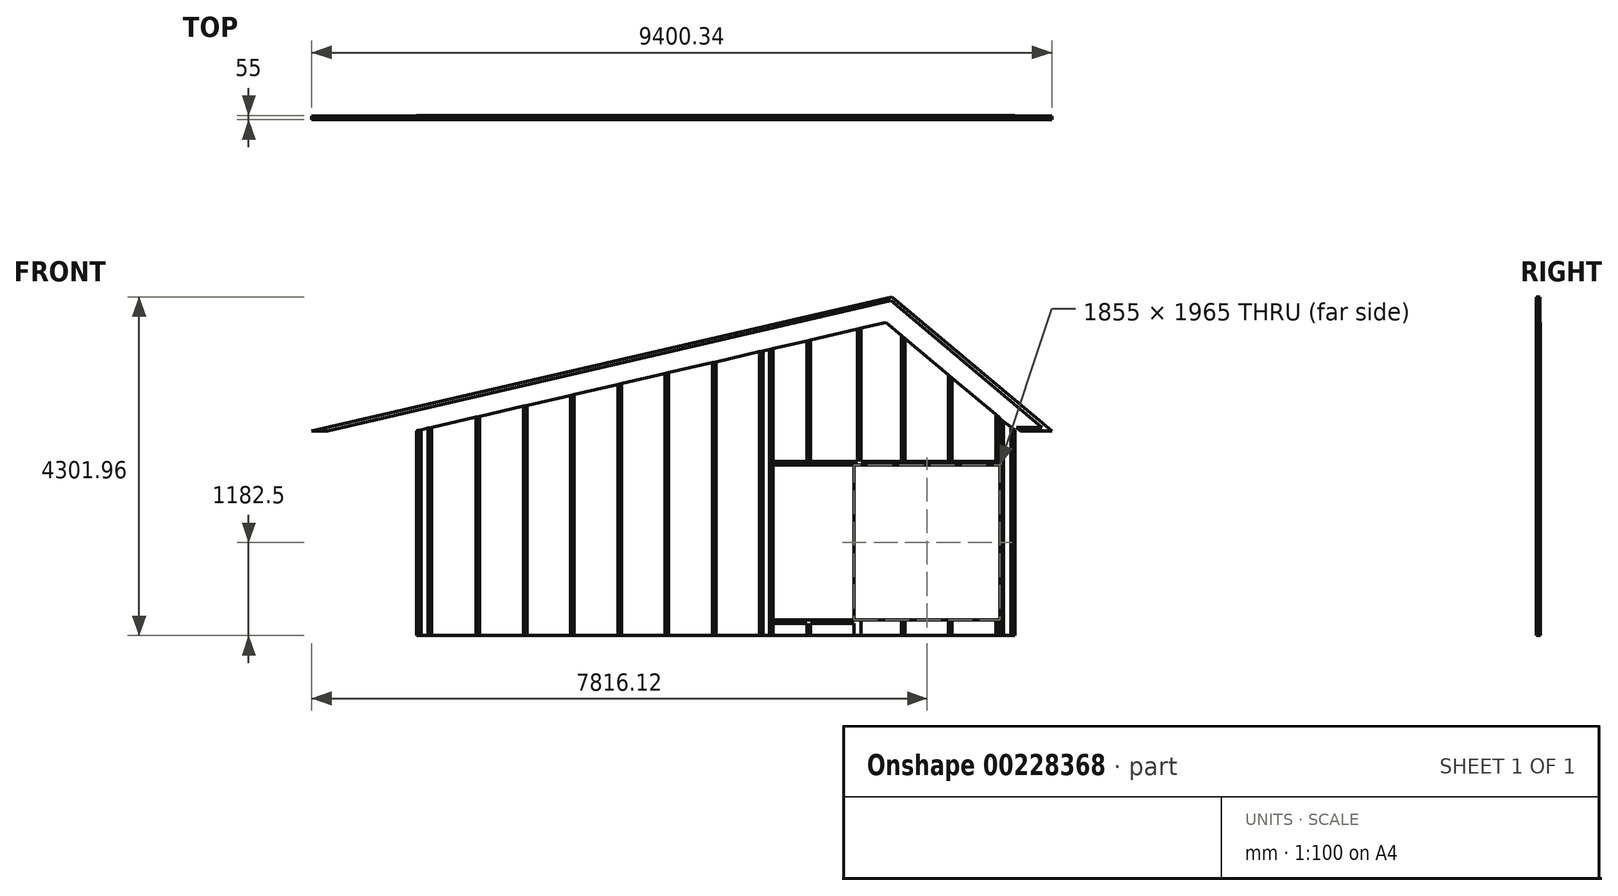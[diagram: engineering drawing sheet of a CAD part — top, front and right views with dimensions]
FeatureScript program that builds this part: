
annotation { "Feature Type Name" : "Feature", "Feature Type Description" : "" }
export const myFeature = defineFeature(function(context is Context, id is Id, definition is map)
    precondition{}
    {
        {
            var Q0;
            Q0=qCreatedBy(makeId("Front.planeOp"),FACE);
            var sketch = newSketch(context, id + "F0", { "sketchPlane" : qUnion([Q0])});
            skLineSegment(sketch, "E0", {"start": v(0, 2907.9) * mm, "end": v(6038.4, 4301.96) * mm});
            skLineSegment(sketch, "E1", {"start": v(7600, 0) * mm, "end": v(0, 0) * mm});
            skLineSegment(sketch, "E2", {"start": v(200, 0) * mm, "end": v(200, 2646.17) * mm});
            skLineSegment(sketch, "E3", {"start": v(0, 2600) * mm, "end": v(5960.14, 3976) * mm});
            skLineSegment(sketch, "E4", {"start": v(5960.14, 3976) * mm, "end": v(7600, 2600) * mm});
            skLineSegment(sketch, "E5", {"start": v(7445, 200) * mm, "end": v(200, 200) * mm});
            skLineSegment(sketch, "E6", {"start": v(0, 2907.9) * mm, "end": v(-1333.62, 2600) * mm});
            skLineSegment(sketch, "E7", {"start": v(-1333.62, 2600) * mm, "end": v(0, 2600) * mm});
            skLineSegment(sketch, "E8", {"start": v(755, 200) * mm, "end": v(755, 2774.3) * mm});
            skLineSegment(sketch, "E9", {"start": v(755, 2774.3) * mm, "end": v(800, 2784.7) * mm});
            skLineSegment(sketch, "E10", {"start": v(800, 2784.7) * mm, "end": v(800, 200) * mm});
            skLineSegment(sketch, "E11", {"start": v(1355, 2912.83) * mm, "end": v(1355, 200) * mm});
            skLineSegment(sketch, "E12", {"start": v(1400, 2923.22) * mm, "end": v(1400, 200) * mm});
            skLineSegment(sketch, "E13", {"start": v(1955, 3051.35) * mm, "end": v(1955, 200) * mm});
            skLineSegment(sketch, "E14", {"start": v(2000, 3061.74) * mm, "end": v(2000, 200) * mm});
            skLineSegment(sketch, "E15", {"start": v(2555, 3189.87) * mm, "end": v(2555, 200) * mm});
            skLineSegment(sketch, "E16", {"start": v(2600, 200) * mm, "end": v(2600, 3200.26) * mm});
            skLineSegment(sketch, "E17", {"start": v(3755, 3466.91) * mm, "end": v(3755, 200) * mm});
            skLineSegment(sketch, "E18", {"start": v(3800, 200) * mm, "end": v(3800, 3477.3) * mm});
            skLineSegment(sketch, "E19", {"start": v(3155, 3328.39) * mm, "end": v(3155, 200) * mm});
            skLineSegment(sketch, "E20", {"start": v(3200, 200) * mm, "end": v(3200, 3338.78) * mm});
            skLineSegment(sketch, "E21", {"start": v(4355, 3605.43) * mm, "end": v(4355, 200) * mm});
            skLineSegment(sketch, "E22", {"start": v(4400, 3615.82) * mm, "end": v(4400, 200) * mm});
            skLineSegment(sketch, "E23", {"start": v(4955, 200) * mm, "end": v(4955, 3743.95) * mm});
            skLineSegment(sketch, "E24", {"start": v(5000, 3754.34) * mm, "end": v(5000, 200) * mm});
            skLineSegment(sketch, "E25", {"start": v(5555, 3882.47) * mm, "end": v(5555, 200) * mm});
            skLineSegment(sketch, "E26", {"start": v(5600, 200) * mm, "end": v(5600, 3892.86) * mm});
            skLineSegment(sketch, "E27", {"start": v(6155, 3812.5) * mm, "end": v(6155, 200) * mm});
            skLineSegment(sketch, "E28", {"start": v(6200, 3774.74) * mm, "end": v(6200, 200) * mm});
            skLineSegment(sketch, "E29", {"start": v(6755, 200) * mm, "end": v(6755, 3309.04) * mm});
            skLineSegment(sketch, "E30", {"start": v(6800, 3271.28) * mm, "end": v(6800, 200) * mm});
            skLineSegment(sketch, "E31", {"start": v(7355, 200) * mm, "end": v(7355, 2805.58) * mm});
            skLineSegment(sketch, "E32", {"start": v(7400, 2767.82) * mm, "end": v(7400, 200) * mm});
            skLineSegment(sketch, "E33", {"start": v(-1133.58, 2600) * mm, "end": v(6026.66, 4253.07) * mm});
            skLineSegment(sketch, "E34", {"start": v(200, 155) * mm, "end": v(7445, 155) * mm});
            skLineSegment(sketch, "E35", {"start": v(7445, 45) * mm, "end": v(200, 45) * mm});
            skLineSegment(sketch, "E36", {"start": v(-938.66, 2645) * mm, "end": v(-5.13, 2645) * mm});
            skLineSegment(sketch, "E37", {"start": v(-5.13, 2645) * mm, "end": v(5971.88, 4024.9) * mm});
            skLineSegment(sketch, "E38", {"start": v(0, 2600) * mm, "end": v(0, 0) * mm});
            skLineSegment(sketch, "E39", {"start": v(45, 0) * mm, "end": v(45, 2610.39) * mm});
            skLineSegment(sketch, "E40", {"start": v(155, 0) * mm, "end": v(155, 2635.78) * mm});
            skLineSegment(sketch, "E41.trimOffspring", {"start": v(7600, 2600) * mm, "end": v(7600, 0) * mm});
            skLineSegment(sketch, "E42", {"start": v(7445, 0) * mm, "end": v(7445, 2730.06) * mm});
            skLineSegment(sketch, "E43", {"start": v(7555, 0) * mm, "end": v(7555, 2637.76) * mm});
            skLineSegment(sketch, "E44", {"start": v(6038.4, 4301.96) * mm, "end": v(8066.72, 2600) * mm});
            skLineSegment(sketch, "E45", {"start": v(8066.72, 2600) * mm, "end": v(7600, 2600) * mm});
            skLineSegment(sketch, "E46", {"start": v(6026.66, 4253.07) * mm, "end": v(7996.7, 2600) * mm});
            skLineSegment(sketch, "E47", {"start": v(5971.88, 4024.9) * mm, "end": v(7670, 2600) * mm});
            skLineSegment(sketch, "E48", {"start": v(7616.38, 2645) * mm, "end": v(7943.08, 2645) * mm});
            skLineSegment(sketch, "E49", {"start": v(6038.4, 4301.96) * mm, "end": v(5960.14, 3976) * mm});
            skSolve(sketch);
        }
        {
            var Q0;
            {var subQ0=sQuery(id+"F0.wireOp",EDGE,"E31");Q0=makeQuery(id+"F0.imprint","IMPRINT",FACE,{"disambiguationData":[TD([[makeQuery(id+"F0.imprint","IMPRINT",EDGE,{"derivedFrom":subQ0}),-1.0]])]});}
            var Q1;
            {var subQ0=sQuery(id+"F0.wireOp",EDGE,"E13");Q1=makeQuery(id+"F0.imprint","IMPRINT",FACE,{"disambiguationData":[TD([[makeQuery(id+"F0.imprint","IMPRINT",EDGE,{"derivedFrom":subQ0}),1.0]])]});}
            var Q2;
            {var subQ0=sQuery(id+"F0.wireOp",EDGE,"E17");Q2=makeQuery(id+"F0.imprint","IMPRINT",FACE,{"disambiguationData":[TD([[makeQuery(id+"F0.imprint","IMPRINT",EDGE,{"derivedFrom":subQ0}),-1.0]])]});}
            var Q3;
            {var subQ2=sQuery(id+"F0.wireOp",EDGE,"E25");Q3=makeQuery(id+"F0.imprint","IMPRINT",FACE,{"disambiguationData":[TD([[makeQuery(id+"F0.imprint","IMPRINT",EDGE,{"derivedFrom":subQ2}),1.0]])]});}
            var Q4;
            {var subQ0=sQuery(id+"F0.wireOp",EDGE,"E18");Q4=makeQuery(id+"F0.imprint","IMPRINT",FACE,{"disambiguationData":[TD([[makeQuery(id+"F0.imprint","IMPRINT",EDGE,{"derivedFrom":subQ0}),-1.0]])]});}
            var Q5;
            {var subQ0=sQuery(id+"F0.wireOp",EDGE,"E14");Q5=makeQuery(id+"F0.imprint","IMPRINT",FACE,{"disambiguationData":[TD([[makeQuery(id+"F0.imprint","IMPRINT",EDGE,{"derivedFrom":subQ0}),1.0]])]});}
            var Q6;
            {var subQ5=sQuery(id+"F0.wireOp",EDGE,"E8");Q6=makeQuery(id+"F0.imprint","IMPRINT",FACE,{"disambiguationData":[TD([[makeQuery(id+"F0.imprint","IMPRINT",EDGE,{"derivedFrom":subQ5}),1.0]])]});}
            var Q7;
            {var subQ0=sQuery(id+"F0.wireOp",EDGE,"E28");Q7=makeQuery(id+"F0.imprint","IMPRINT",FACE,{"disambiguationData":[TD([[makeQuery(id+"F0.imprint","IMPRINT",EDGE,{"derivedFrom":subQ0}),1.0]])]});}
            var Q8;
            {var subQ0=sQuery(id+"F0.wireOp",EDGE,"E30");Q8=makeQuery(id+"F0.imprint","IMPRINT",FACE,{"disambiguationData":[TD([[makeQuery(id+"F0.imprint","IMPRINT",EDGE,{"derivedFrom":subQ0}),1.0]])]});}
            var Q9;
            {var subQ0=sQuery(id+"F0.wireOp",EDGE,"E26");Q9=makeQuery(id+"F0.imprint","IMPRINT",FACE,{"disambiguationData":[TD([[makeQuery(id+"F0.imprint","IMPRINT",EDGE,{"derivedFrom":subQ0}),-1.0]])]});}
            var Q10;
            {var subQ0=sQuery(id+"F0.wireOp",EDGE,"E16");Q10=makeQuery(id+"F0.imprint","IMPRINT",FACE,{"disambiguationData":[TD([[makeQuery(id+"F0.imprint","IMPRINT",EDGE,{"derivedFrom":subQ0}),-1.0]])]});}
            var Q11;
            {var subQ0=sQuery(id+"F0.wireOp",EDGE,"E12");Q11=makeQuery(id+"F0.imprint","IMPRINT",FACE,{"disambiguationData":[TD([[makeQuery(id+"F0.imprint","IMPRINT",EDGE,{"derivedFrom":subQ0}),1.0]])]});}
            var Q12;
            {var subQ0=sQuery(id+"F0.wireOp",EDGE,"E24");Q12=makeQuery(id+"F0.imprint","IMPRINT",FACE,{"disambiguationData":[TD([[makeQuery(id+"F0.imprint","IMPRINT",EDGE,{"derivedFrom":subQ0}),1.0]])]});}
            var Q13;
            {var subQ0=sQuery(id+"F0.wireOp",EDGE,"E17");Q13=makeQuery(id+"F0.imprint","IMPRINT",FACE,{"disambiguationData":[TD([[makeQuery(id+"F0.imprint","IMPRINT",EDGE,{"derivedFrom":subQ0}),1.0]])]});}
            var Q14;
            {var subQ0=sQuery(id+"F0.wireOp",EDGE,"E10");Q14=makeQuery(id+"F0.imprint","IMPRINT",FACE,{"disambiguationData":[TD([[makeQuery(id+"F0.imprint","IMPRINT",EDGE,{"derivedFrom":subQ0}),1.0]])]});}
            var Q15;
            {var subQ0=sQuery(id+"F0.wireOp",EDGE,"E22");Q15=makeQuery(id+"F0.imprint","IMPRINT",FACE,{"disambiguationData":[TD([[makeQuery(id+"F0.imprint","IMPRINT",EDGE,{"derivedFrom":subQ0}),1.0]])]});}
            var Q16;
            {var subQ0=sQuery(id+"F0.wireOp",EDGE,"E11");Q16=makeQuery(id+"F0.imprint","IMPRINT",FACE,{"disambiguationData":[TD([[makeQuery(id+"F0.imprint","IMPRINT",EDGE,{"derivedFrom":subQ0}),1.0]])]});}
            var Q17;
            {var subQ2=sQuery(id+"F0.wireOp",EDGE,"E23");Q17=makeQuery(id+"F0.imprint","IMPRINT",FACE,{"disambiguationData":[TD([[makeQuery(id+"F0.imprint","IMPRINT",EDGE,{"derivedFrom":subQ2}),-1.0]])]});}
            var Q18;
            {var subQ0=sQuery(id+"F0.wireOp",EDGE,"E21");Q18=makeQuery(id+"F0.imprint","IMPRINT",FACE,{"disambiguationData":[TD([[makeQuery(id+"F0.imprint","IMPRINT",EDGE,{"derivedFrom":subQ0}),1.0]])]});}
            var Q19;
            {var subQ0=sQuery(id+"F0.wireOp",EDGE,"E19");Q19=makeQuery(id+"F0.imprint","IMPRINT",FACE,{"disambiguationData":[TD([[makeQuery(id+"F0.imprint","IMPRINT",EDGE,{"derivedFrom":subQ0}),1.0]])]});}
            var Q20;
            {var subQ2=sQuery(id+"F0.wireOp",EDGE,"E29");Q20=makeQuery(id+"F0.imprint","IMPRINT",FACE,{"disambiguationData":[TD([[makeQuery(id+"F0.imprint","IMPRINT",EDGE,{"derivedFrom":subQ2}),-1.0]])]});}
            var Q21;
            {var subQ2=sQuery(id+"F0.wireOp",EDGE,"E27");Q21=makeQuery(id+"F0.imprint","IMPRINT",FACE,{"disambiguationData":[TD([[makeQuery(id+"F0.imprint","IMPRINT",EDGE,{"derivedFrom":subQ2}),1.0]])]});}
            var Q22;
            {var subQ0=sQuery(id+"F0.wireOp",EDGE,"E8");Q22=makeQuery(id+"F0.imprint","IMPRINT",FACE,{"disambiguationData":[TD([[makeQuery(id+"F0.imprint","IMPRINT",EDGE,{"derivedFrom":subQ0}),-1.0]])]});}
            var Q23;
            {var subQ0=sQuery(id+"F0.wireOp",EDGE,"E15");Q23=makeQuery(id+"F0.imprint","IMPRINT",FACE,{"disambiguationData":[TD([[makeQuery(id+"F0.imprint","IMPRINT",EDGE,{"derivedFrom":subQ0}),1.0]])]});}
            var Q24;
            {var subQ6=sQuery(id+"F0.wireOp",EDGE,"E40");Q24=makeQuery(id+"F0.imprint","IMPRINT",FACE,{"disambiguationData":[TD([[makeQuery(id+"F0.imprint","IMPRINT",EDGE,{"derivedFrom":subQ6}),-1.0]])]});}
            var Q25;
            {var subQ0=sQuery(id+"F0.wireOp",EDGE,"E39");Q25=makeQuery(id+"F0.imprint","IMPRINT",FACE,{"disambiguationData":[TD([[makeQuery(id+"F0.imprint","IMPRINT",EDGE,{"derivedFrom":subQ0}),-1.0]])]});}
            var Q26;
            {var subQ0=sQuery(id+"F0.wireOp",EDGE,"E38");Q26=makeQuery(id+"F0.imprint","IMPRINT",FACE,{"disambiguationData":[TD([[makeQuery(id+"F0.imprint","IMPRINT",EDGE,{"derivedFrom":subQ0}),1.0]])]});}
            var Q27;
            {var subQ6=sQuery(id+"F0.wireOp",EDGE,"E43");Q27=makeQuery(id+"F0.imprint","IMPRINT",FACE,{"disambiguationData":[TD([[makeQuery(id+"F0.imprint","IMPRINT",EDGE,{"derivedFrom":subQ6}),1.0]])]});}
            var Q28;
            {var subQ0=sQuery(id+"F0.wireOp",EDGE,"E32");Q28=makeQuery(id+"F0.imprint","IMPRINT",FACE,{"disambiguationData":[TD([[makeQuery(id+"F0.imprint","IMPRINT",EDGE,{"derivedFrom":subQ0}),1.0]])]});}
            var Q29;
            {var subQ2=sQuery(id+"F0.wireOp",EDGE,"E41.trimOffspring");Q29=makeQuery(id+"F0.imprint","IMPRINT",FACE,{"disambiguationData":[TD([[makeQuery(id+"F0.imprint","IMPRINT",EDGE,{"derivedFrom":subQ2}),-1.0]])]});}
            var Q30;
            {var subQ10=sQuery(id+"F0.wireOp",EDGE,"E34");Q30=makeQuery(id+"F0.imprint","IMPRINT",FACE,{"disambiguationData":[TD([[makeQuery(id+"F0.imprint","IMPRINT",EDGE,{"derivedFrom":subQ10}),1.0]])]});}
            var Q31;
            {var subQ2=sQuery(id+"F0.wireOp",EDGE,"E34");Q31=makeQuery(id+"F0.imprint","IMPRINT",FACE,{"disambiguationData":[TD([[makeQuery(id+"F0.imprint","IMPRINT",EDGE,{"derivedFrom":subQ2}),-1.0]])]});}
            var Q32;
            {var subQ5=sQuery(id+"F0.wireOp",EDGE,"E35");Q32=makeQuery(id+"F0.imprint","IMPRINT",FACE,{"disambiguationData":[TD([[makeQuery(id+"F0.imprint","IMPRINT",EDGE,{"derivedFrom":subQ5}),1.0]])]});}
            extrude(context, id + "F1", {"entities" : qUnion([Q0, Q1, Q2, Q3, Q4, Q5, Q6, Q7, Q8, Q9, Q10, Q11, Q12, Q13, Q14, Q15, Q16, Q17, Q18, Q19, Q20, Q21, Q22, Q23, Q24, Q25, Q26, Q27, Q28, Q29, Q30, Q31, Q32]), "depth" : 10 * mm, "offsetDistance" : 25 * mm});
        }
        {
            var Q0;
            Q0=makeQuery(id+"F1.opExtrude","CAP_FACE",FACE,{"disambiguationData":[OSD([sQuery(id+"F0.wireOp",EDGE,"E0"),sQuery(id+"F0.wireOp",EDGE,"E1"),sQuery(id+"F0.wireOp",EDGE,"E6"),sQuery(id+"F0.wireOp",EDGE,"E7"),sQuery(id+"F0.wireOp",EDGE,"E38"),sQuery(id+"F0.wireOp",EDGE,"E41.trimOffspring"),sQuery(id+"F0.wireOp",EDGE,"E44"),sQuery(id+"F0.wireOp",EDGE,"E45")])],"isStart":false});
            var sketch = newSketch(context, id + "F2", { "sketchPlane" : qUnion([Q0])});
            skLineSegment(sketch, "E50", {"start": v(0, 2907.9) * mm, "end": v(6038.4, 4301.96) * mm});
            skLineSegment(sketch, "E51", {"start": v(7600, 0) * mm, "end": v(0, 0) * mm});
            skLineSegment(sketch, "E52", {"start": v(200, 0) * mm, "end": v(200, 2646.17) * mm});
            skLineSegment(sketch, "E53", {"start": v(0, 2600) * mm, "end": v(5960.14, 3976) * mm});
            skLineSegment(sketch, "E54", {"start": v(5960.14, 3976) * mm, "end": v(7600, 2600) * mm});
            skLineSegment(sketch, "E55", {"start": v(0, 2907.9) * mm, "end": v(-1333.62, 2600) * mm});
            skLineSegment(sketch, "E56", {"start": v(-1333.62, 2600) * mm, "end": v(0, 2600) * mm});
            skLineSegment(sketch, "E57", {"start": v(755, 0) * mm, "end": v(755, 2774.3) * mm});
            skLineSegment(sketch, "E58", {"start": v(755, 2774.3) * mm, "end": v(800, 2784.7) * mm});
            skLineSegment(sketch, "E59", {"start": v(800, 2784.7) * mm, "end": v(800, 0) * mm});
            skLineSegment(sketch, "E60", {"start": v(1355, 2912.83) * mm, "end": v(1355, 0) * mm});
            skLineSegment(sketch, "E61", {"start": v(1400, 2923.22) * mm, "end": v(1400, 0) * mm});
            skLineSegment(sketch, "E62", {"start": v(1955, 3051.35) * mm, "end": v(1955, 0) * mm});
            skLineSegment(sketch, "E63", {"start": v(2000, 3061.74) * mm, "end": v(2000, 0) * mm});
            skLineSegment(sketch, "E64", {"start": v(2555, 3189.87) * mm, "end": v(2555, 0) * mm});
            skLineSegment(sketch, "E65", {"start": v(2600, 0) * mm, "end": v(2600, 3200.26) * mm});
            skLineSegment(sketch, "E66", {"start": v(3755, 3466.91) * mm, "end": v(3755, 0) * mm});
            skLineSegment(sketch, "E67", {"start": v(3800, 0) * mm, "end": v(3800, 3477.3) * mm});
            skLineSegment(sketch, "E68", {"start": v(3155, 3328.39) * mm, "end": v(3155, 0) * mm});
            skLineSegment(sketch, "E69", {"start": v(3200, 0) * mm, "end": v(3200, 3338.78) * mm});
            skLineSegment(sketch, "E70", {"start": v(4355, 3605.43) * mm, "end": v(4355, 0) * mm});
            skLineSegment(sketch, "E71", {"start": v(4400, 3615.82) * mm, "end": v(4400, 0) * mm});
            skLineSegment(sketch, "E72", {"start": v(4955, 0) * mm, "end": v(4955, 3743.95) * mm});
            skLineSegment(sketch, "E73", {"start": v(5000, 3754.34) * mm, "end": v(5000, 0) * mm});
            skLineSegment(sketch, "E74", {"start": v(5555, 3882.47) * mm, "end": v(5555, 0) * mm});
            skLineSegment(sketch, "E75", {"start": v(5600, 0) * mm, "end": v(5600, 3892.86) * mm});
            skLineSegment(sketch, "E76", {"start": v(6155, 3812.5) * mm, "end": v(6155, 0) * mm});
            skLineSegment(sketch, "E77", {"start": v(6200, 3774.74) * mm, "end": v(6200, 0) * mm});
            skLineSegment(sketch, "E78", {"start": v(6755, 0) * mm, "end": v(6755, 3309.04) * mm});
            skLineSegment(sketch, "E79", {"start": v(6800, 3271.28) * mm, "end": v(6800, 0) * mm});
            skLineSegment(sketch, "E80", {"start": v(7355, 0) * mm, "end": v(7355, 2805.58) * mm});
            skLineSegment(sketch, "E81", {"start": v(7400, 2767.82) * mm, "end": v(7400, 0) * mm});
            skLineSegment(sketch, "E82", {"start": v(-1133.58, 2600) * mm, "end": v(6026.66, 4253.07) * mm});
            skLineSegment(sketch, "E83", {"start": v(-938.66, 2645) * mm, "end": v(-5.13, 2645) * mm});
            skLineSegment(sketch, "E84", {"start": v(-5.13, 2645) * mm, "end": v(5971.88, 4024.9) * mm});
            skLineSegment(sketch, "E85", {"start": v(0, 2600) * mm, "end": v(0, 0) * mm});
            skLineSegment(sketch, "E86", {"start": v(55, 0) * mm, "end": v(55, 2612.7) * mm});
            skLineSegment(sketch, "E87", {"start": v(145, 0) * mm, "end": v(145, 2633.48) * mm});
            skLineSegment(sketch, "E88.trimOffspring", {"start": v(7600, 2600) * mm, "end": v(7600, 0) * mm});
            skLineSegment(sketch, "E89", {"start": v(7455, 0) * mm, "end": v(7455, 2721.67) * mm});
            skLineSegment(sketch, "E90", {"start": v(6038.4, 4301.96) * mm, "end": v(8066.72, 2600) * mm});
            skLineSegment(sketch, "E91", {"start": v(8066.72, 2600) * mm, "end": v(7600, 2600) * mm});
            skLineSegment(sketch, "E92", {"start": v(6026.66, 4253.07) * mm, "end": v(7996.7, 2600) * mm});
            skLineSegment(sketch, "E93", {"start": v(5971.88, 4024.9) * mm, "end": v(7670, 2600) * mm});
            skLineSegment(sketch, "E94", {"start": v(7616.38, 2645) * mm, "end": v(7943.08, 2645) * mm});
            skLineSegment(sketch, "E95", {"start": v(7400, 1090) * mm, "end": v(5645, 1090) * mm});
            skLineSegment(sketch, "E96", {"start": v(4525, 2165) * mm, "end": v(7410, 2165) * mm});
            skLineSegment(sketch, "E97", {"start": v(7410, 2210) * mm, "end": v(4525, 2210) * mm});
            skLineSegment(sketch, "E98", {"start": v(5645, 3903.25) * mm, "end": v(5645, 0) * mm});
            skLineSegment(sketch, "E99", {"start": v(5645, 1045) * mm, "end": v(7400, 1045) * mm});
            skLineSegment(sketch, "E100", {"start": v(4525, 3644.68) * mm, "end": v(4525, 0) * mm});
            skLineSegment(sketch, "E101", {"start": v(4480, 3634.29) * mm, "end": v(4480, 0) * mm});
            skLineSegment(sketch, "E102", {"start": v(4525, 200) * mm, "end": v(5555, 200) * mm});
            skLineSegment(sketch, "E103", {"start": v(5555, 155) * mm, "end": v(4525, 155) * mm});
            skLineSegment(sketch, "E104", {"start": v(10, 2602.3) * mm, "end": v(10, 0) * mm});
            skLineSegment(sketch, "E105", {"start": v(10, 0) * mm, "end": v(190, 0) * mm});
            skLineSegment(sketch, "E106", {"start": v(190, 0) * mm, "end": v(190, 2643.86) * mm});
            skLineSegment(sketch, "E107", {"start": v(745, 2772) * mm, "end": v(745, 0) * mm});
            skLineSegment(sketch, "E108", {"start": v(810, 0) * mm, "end": v(810, 2787) * mm});
            skLineSegment(sketch, "E109", {"start": v(1345, 2910.52) * mm, "end": v(1345, 0) * mm});
            skLineSegment(sketch, "E110", {"start": v(1410, 2925.52) * mm, "end": v(1410, 0) * mm});
            skLineSegment(sketch, "E111", {"start": v(1945, 3049.04) * mm, "end": v(1945, 0) * mm});
            skLineSegment(sketch, "E112", {"start": v(2010, 3064.05) * mm, "end": v(2010, 0) * mm});
            skLineSegment(sketch, "E113", {"start": v(2545, 3187.56) * mm, "end": v(2545, 0) * mm});
            skLineSegment(sketch, "E114", {"start": v(2610, 3202.57) * mm, "end": v(2610, 0) * mm});
            skLineSegment(sketch, "E115", {"start": v(3145, 3326.08) * mm, "end": v(3145, 0) * mm});
            skLineSegment(sketch, "E116", {"start": v(3210, 3341.09) * mm, "end": v(3210, 0) * mm});
            skLineSegment(sketch, "E117", {"start": v(3745, 3464.6) * mm, "end": v(3745, 0) * mm});
            skLineSegment(sketch, "E118", {"start": v(3810, 3479.6) * mm, "end": v(3810, 0) * mm});
            skLineSegment(sketch, "E119", {"start": v(4345, 3603.12) * mm, "end": v(4345, 0) * mm});
            skLineSegment(sketch, "E120", {"start": v(4410, 0) * mm, "end": v(4410, 3618.13) * mm});
            skLineSegment(sketch, "E121", {"start": v(4470, 3631.98) * mm, "end": v(4470, 0) * mm});
            skLineSegment(sketch, "E122", {"start": v(4535, 0) * mm, "end": v(4535, 3646.99) * mm});
            skLineSegment(sketch, "E123", {"start": v(4535, 2220) * mm, "end": v(7410, 2220) * mm});
            skLineSegment(sketch, "E124", {"start": v(5645, 2155) * mm, "end": v(7410, 2155) * mm});
            skLineSegment(sketch, "E125", {"start": v(5645, 1100) * mm, "end": v(7400, 1100) * mm});
            skLineSegment(sketch, "E126", {"start": v(5655, 2155) * mm, "end": v(5655, 1100) * mm});
            skLineSegment(sketch, "E127", {"start": v(5655, 1045) * mm, "end": v(5655, 0) * mm});
            skLineSegment(sketch, "E128", {"start": v(7345, 1045) * mm, "end": v(7345, 0) * mm});
            skLineSegment(sketch, "E129", {"start": v(6145, 1045) * mm, "end": v(6145, 0) * mm});
            skLineSegment(sketch, "E130", {"start": v(6210, 1045) * mm, "end": v(6210, 0) * mm});
            skLineSegment(sketch, "E131", {"start": v(6745, 1045) * mm, "end": v(6745, 0) * mm});
            skLineSegment(sketch, "E132", {"start": v(6810, 1045) * mm, "end": v(6810, 0) * mm});
            skLineSegment(sketch, "E133", {"start": v(4945, 3741.64) * mm, "end": v(4945, 2220) * mm});
            skLineSegment(sketch, "E134", {"start": v(5010, 3756.65) * mm, "end": v(5010, 2220) * mm});
            skLineSegment(sketch, "E135", {"start": v(5545, 3880.16) * mm, "end": v(5545, 2220) * mm});
            skLineSegment(sketch, "E136", {"start": v(5655, 3905.56) * mm, "end": v(5655, 2220) * mm});
            skLineSegment(sketch, "E137", {"start": v(6145, 3820.89) * mm, "end": v(6145, 2220) * mm});
            skLineSegment(sketch, "E138", {"start": v(6210, 3766.35) * mm, "end": v(6210, 2220) * mm});
            skLineSegment(sketch, "E139", {"start": v(6745, 3317.43) * mm, "end": v(6745, 2220) * mm});
            skLineSegment(sketch, "E140", {"start": v(6810, 3262.89) * mm, "end": v(6810, 2220) * mm});
            skLineSegment(sketch, "E141", {"start": v(5555, 2155) * mm, "end": v(4535, 2155) * mm});
            skLineSegment(sketch, "E142", {"start": v(5555, 210) * mm, "end": v(4535, 210) * mm});
            skLineSegment(sketch, "E143", {"start": v(5545, 2155) * mm, "end": v(5545, 210) * mm});
            skLineSegment(sketch, "E144", {"start": v(4945, 155) * mm, "end": v(4945, 0) * mm});
            skLineSegment(sketch, "E145", {"start": v(5010, 155) * mm, "end": v(5010, 0) * mm});
            skLineSegment(sketch, "E146", {"start": v(4535, 145) * mm, "end": v(4945, 145) * mm});
            skLineSegment(sketch, "E147", {"start": v(5010, 145) * mm, "end": v(5555, 145) * mm});
            skLineSegment(sketch, "E148", {"start": v(5655, 1035) * mm, "end": v(6145, 1035) * mm});
            skLineSegment(sketch, "E149", {"start": v(6210, 1035) * mm, "end": v(6745, 1035) * mm});
            skLineSegment(sketch, "E150", {"start": v(6810, 1035) * mm, "end": v(7345, 1035) * mm});
            skLineSegment(sketch, "E151", {"start": v(7410, 2759.43) * mm, "end": v(7410, 0) * mm});
            skLineSegment(sketch, "E152", {"start": v(7600, 0) * mm, "end": v(7590, 0) * mm});
            skLineSegment(sketch, "E153", {"start": v(7590, 0) * mm, "end": v(7590, 2608.4) * mm});
            skLineSegment(sketch, "E154", {"start": v(7590, 0) * mm, "end": v(7545, 0) * mm});
            skLineSegment(sketch, "E155", {"start": v(7545, 0) * mm, "end": v(7545, 2646.15) * mm});
            skSolve(sketch);
        }
        {
            var Q0;
            {var subQ0=sQuery(id+"F2.wireOp",EDGE,"E74");Q0=makeQuery(id+"F2.imprint","IMPRINT",FACE,{"disambiguationData":[TD([[makeQuery(id+"F2.imprint","IMPRINT",EDGE,{"derivedFrom":subQ0}),1.0]])]});}
            var Q1;
            {var subQ0=sQuery(id+"F2.wireOp",EDGE,"E70");Q1=makeQuery(id+"F2.imprint","IMPRINT",FACE,{"disambiguationData":[TD([[makeQuery(id+"F2.imprint","IMPRINT",EDGE,{"derivedFrom":subQ0}),1.0]])]});}
            var Q2;
            {var subQ0=sQuery(id+"F2.wireOp",EDGE,"E66");Q2=makeQuery(id+"F2.imprint","IMPRINT",FACE,{"disambiguationData":[TD([[makeQuery(id+"F2.imprint","IMPRINT",EDGE,{"derivedFrom":subQ0}),1.0]])]});}
            var Q3;
            {var subQ0=sQuery(id+"F2.wireOp",EDGE,"E68");Q3=makeQuery(id+"F2.imprint","IMPRINT",FACE,{"disambiguationData":[TD([[makeQuery(id+"F2.imprint","IMPRINT",EDGE,{"derivedFrom":subQ0}),1.0]])]});}
            var Q4;
            {var subQ0=sQuery(id+"F2.wireOp",EDGE,"E64");Q4=makeQuery(id+"F2.imprint","IMPRINT",FACE,{"disambiguationData":[TD([[makeQuery(id+"F2.imprint","IMPRINT",EDGE,{"derivedFrom":subQ0}),1.0]])]});}
            var Q5;
            {var subQ0=sQuery(id+"F2.wireOp",EDGE,"E62");Q5=makeQuery(id+"F2.imprint","IMPRINT",FACE,{"disambiguationData":[TD([[makeQuery(id+"F2.imprint","IMPRINT",EDGE,{"derivedFrom":subQ0}),1.0]])]});}
            var Q6;
            {var subQ0=sQuery(id+"F2.wireOp",EDGE,"E60");Q6=makeQuery(id+"F2.imprint","IMPRINT",FACE,{"disambiguationData":[TD([[makeQuery(id+"F2.imprint","IMPRINT",EDGE,{"derivedFrom":subQ0}),1.0]])]});}
            var Q7;
            {var subQ0=sQuery(id+"F2.wireOp",EDGE,"E57");Q7=makeQuery(id+"F2.imprint","IMPRINT",FACE,{"disambiguationData":[TD([[makeQuery(id+"F2.imprint","IMPRINT",EDGE,{"derivedFrom":subQ0}),-1.0]])]});}
            var Q8;
            Q8=makeQuery(id+"F2.imprint","IMPRINT",FACE,{"disambiguationData":[TD([[makeQuery(id+"F2.imprint","IMPRINT",EDGE,{"derivedFrom":sQuery(id+"F2.wireOp",EDGE,"E50")}),-1.0]])]});
            var Q9;
            {var subQ3=sQuery(id+"F2.wireOp",EDGE,"AWjpgJo8-LtKh-493l-jI3X-VLIllok5Xs9P");Q9=makeQuery(id+"F2.imprint","IMPRINT",FACE,{"disambiguationData":[TD([[makeQuery(id+"F2.imprint","IMPRINT",EDGE,{"derivedFrom":subQ3}),1.0]])]});}
            var Q10;
            {var subQ5=sQuery(id+"F2.wireOp",EDGE,"M6yIeqAo-Q4vC-dqGf-9kuj-Eh7sLFh62U3w");Q10=makeQuery(id+"F2.imprint","IMPRINT",FACE,{"disambiguationData":[TD([[makeQuery(id+"F2.imprint","IMPRINT",EDGE,{"derivedFrom":subQ5}),-1.0]])]});}
            var Q11;
            {var subQ5=sQuery(id+"F2.wireOp",EDGE,"E94");Q11=makeQuery(id+"F2.imprint","IMPRINT",FACE,{"disambiguationData":[TD([[makeQuery(id+"F2.imprint","IMPRINT",EDGE,{"derivedFrom":subQ5}),-1.0]])]});}
            var Q12;
            {var subQ5=sQuery(id+"F2.wireOp",EDGE,"taZ2oKkk-BtzL-6bV4-5qbK-Knkht85AcqPx");Q12=makeQuery(id+"F2.imprint","IMPRINT",FACE,{"disambiguationData":[TD([[makeQuery(id+"F2.imprint","IMPRINT",EDGE,{"derivedFrom":subQ5}),1.0]])]});}
            var Q13;
            {var subQ7=sQuery(id+"F2.wireOp",EDGE,"E101");Q13=makeQuery(id+"F2.imprint","IMPRINT",FACE,{"disambiguationData":[TD([[makeQuery(id+"F2.imprint","IMPRINT",EDGE,{"derivedFrom":subQ7}),1.0]])]});}
            var Q14;
            {var subQ0=sQuery(id+"F2.wireOp",EDGE,"E96");var subQ1=sQuery(id+"F2.wireOp",EDGE,"E72");var subQ2=makeQuery(id+"F2.imprint","INTERSECT",VERTEX,{"derivedFrom":[subQ1,subQ0]});Q14=makeQuery(id+"F2.imprint","IMPRINT",FACE,{"disambiguationData":[TD([[makeQuery(id+"F2.imprint","IMPRINT",EDGE,{"disambiguationData":[TD([[subQ2,-1.0]])],"derivedFrom":subQ1}),1.0]])]});}
            var Q15;
            {var subQ0=sQuery(id+"F2.wireOp",EDGE,"E97");var subQ1=sQuery(id+"F2.wireOp",EDGE,"E73");var subQ2=makeQuery(id+"F2.imprint","INTERSECT",VERTEX,{"derivedFrom":[subQ1,subQ0]});Q15=makeQuery(id+"F2.imprint","IMPRINT",FACE,{"disambiguationData":[TD([[makeQuery(id+"F2.imprint","IMPRINT",EDGE,{"disambiguationData":[TD([[subQ2,-1.0]])],"derivedFrom":subQ1}),1.0]])]});}
            var Q16;
            {var subQ0=sQuery(id+"F2.wireOp",EDGE,"E72");var subQ1=sQuery(id+"F2.wireOp",EDGE,"E53");var subQ2=makeQuery(id+"F2.imprint","INTERSECT",VERTEX,{"derivedFrom":[subQ1,subQ0]});Q16=makeQuery(id+"F2.imprint","IMPRINT",FACE,{"disambiguationData":[TD([[makeQuery(id+"F2.imprint","IMPRINT",EDGE,{"disambiguationData":[TD([[subQ2,-1.0]])],"derivedFrom":subQ1}),-1.0]])]});}
            var Q17;
            {var subQ0=sQuery(id+"F2.wireOp",EDGE,"E96");var subQ1=sQuery(id+"F2.wireOp",EDGE,"E72");var subQ2=makeQuery(id+"F2.imprint","INTERSECT",VERTEX,{"derivedFrom":[subQ1,subQ0]});Q17=makeQuery(id+"F2.imprint","IMPRINT",FACE,{"disambiguationData":[TD([[makeQuery(id+"F2.imprint","IMPRINT",EDGE,{"disambiguationData":[TD([[subQ2,-1.0]])],"derivedFrom":subQ1}),-1.0]])]});}
            var Q18;
            {var subQ4=sQuery(id+"F2.wireOp",EDGE,"E75");var subQ6=sQuery(id+"F2.wireOp",EDGE,"38f50c6f-4d65-446f-a054-f236fb353168");var subQ9=makeQuery(id+"F2.imprint","INTERSECT",VERTEX,{"derivedFrom":[subQ4,subQ6]});Q18=makeQuery(id+"F2.imprint","IMPRINT",FACE,{"disambiguationData":[TD([[makeQuery(id+"F2.imprint","IMPRINT",EDGE,{"disambiguationData":[TD([[subQ9,-1.0]])],"derivedFrom":subQ4}),-1.0]])]});}
            var Q19;
            {var subQ0=sQuery(id+"F2.wireOp",EDGE,"E96");var subQ1=sQuery(id+"F2.wireOp",EDGE,"E75");var subQ2=makeQuery(id+"F2.imprint","INTERSECT",VERTEX,{"derivedFrom":[subQ1,subQ0]});Q19=makeQuery(id+"F2.imprint","IMPRINT",FACE,{"disambiguationData":[TD([[makeQuery(id+"F2.imprint","IMPRINT",EDGE,{"disambiguationData":[TD([[subQ2,-1.0]])],"derivedFrom":subQ1}),-1.0]])]});}
            var Q20;
            {var subQ0=sQuery(id+"F2.wireOp",EDGE,"E75");var subQ1=sQuery(id+"F2.wireOp",EDGE,"E53");var subQ2=makeQuery(id+"F2.imprint","INTERSECT",VERTEX,{"derivedFrom":[subQ1,subQ0]});Q20=makeQuery(id+"F2.imprint","IMPRINT",FACE,{"disambiguationData":[TD([[makeQuery(id+"F2.imprint","IMPRINT",EDGE,{"disambiguationData":[TD([[subQ2,-1.0]])],"derivedFrom":subQ1}),-1.0]])]});}
            var Q21;
            {var subQ0=sQuery(id+"F2.wireOp",EDGE,"E97");var subQ1=sQuery(id+"F2.wireOp",EDGE,"E76");var subQ2=makeQuery(id+"F2.imprint","INTERSECT",VERTEX,{"derivedFrom":[subQ1,subQ0]});Q21=makeQuery(id+"F2.imprint","IMPRINT",FACE,{"disambiguationData":[TD([[makeQuery(id+"F2.imprint","IMPRINT",EDGE,{"disambiguationData":[TD([[subQ2,-1.0]])],"derivedFrom":subQ1}),-1.0]])]});}
            var Q22;
            {var subQ0=sQuery(id+"F2.wireOp",EDGE,"E95");var subQ1=sQuery(id+"F2.wireOp",EDGE,"E76");var subQ2=makeQuery(id+"F2.imprint","INTERSECT",VERTEX,{"derivedFrom":[subQ1,subQ0]});Q22=makeQuery(id+"F2.imprint","IMPRINT",FACE,{"disambiguationData":[TD([[makeQuery(id+"F2.imprint","IMPRINT",EDGE,{"disambiguationData":[TD([[subQ2,-1.0]])],"derivedFrom":subQ1}),-1.0]])]});}
            var Q23;
            {var subQ0=sQuery(id+"F2.wireOp",EDGE,"E76");var subQ1=sQuery(id+"F2.wireOp",EDGE,"E54");var subQ2=makeQuery(id+"F2.imprint","INTERSECT",VERTEX,{"derivedFrom":[subQ1,subQ0]});Q23=makeQuery(id+"F2.imprint","IMPRINT",FACE,{"disambiguationData":[TD([[makeQuery(id+"F2.imprint","IMPRINT",EDGE,{"disambiguationData":[TD([[subQ2,-1.0]])],"derivedFrom":subQ1}),-1.0]])]});}
            var Q24;
            {var subQ0=sQuery(id+"F2.wireOp",EDGE,"E97");var subQ1=sQuery(id+"F2.wireOp",EDGE,"E76");var subQ2=makeQuery(id+"F2.imprint","INTERSECT",VERTEX,{"derivedFrom":[subQ1,subQ0]});Q24=makeQuery(id+"F2.imprint","IMPRINT",FACE,{"disambiguationData":[TD([[makeQuery(id+"F2.imprint","IMPRINT",EDGE,{"disambiguationData":[TD([[subQ2,-1.0]])],"derivedFrom":subQ1}),1.0]])]});}
            var Q25;
            {var subQ0=sQuery(id+"F2.wireOp",EDGE,"E95");var subQ1=sQuery(id+"F2.wireOp",EDGE,"E76");var subQ2=makeQuery(id+"F2.imprint","INTERSECT",VERTEX,{"derivedFrom":[subQ1,subQ0]});Q25=makeQuery(id+"F2.imprint","IMPRINT",FACE,{"disambiguationData":[TD([[makeQuery(id+"F2.imprint","IMPRINT",EDGE,{"disambiguationData":[TD([[subQ2,-1.0]])],"derivedFrom":subQ1}),1.0]])]});}
            var Q26;
            {var subQ0=sQuery(id+"F2.wireOp",EDGE,"E78");var subQ1=sQuery(id+"F2.wireOp",EDGE,"E54");var subQ2=makeQuery(id+"F2.imprint","INTERSECT",VERTEX,{"derivedFrom":[subQ1,subQ0]});Q26=makeQuery(id+"F2.imprint","IMPRINT",FACE,{"disambiguationData":[TD([[makeQuery(id+"F2.imprint","IMPRINT",EDGE,{"disambiguationData":[TD([[subQ2,-1.0]])],"derivedFrom":subQ1}),-1.0]])]});}
            var Q27;
            {var subQ0=sQuery(id+"F2.wireOp",EDGE,"E99");var subQ1=sQuery(id+"F2.wireOp",EDGE,"E78");var subQ2=makeQuery(id+"F2.imprint","INTERSECT",VERTEX,{"derivedFrom":[subQ1,subQ0]});Q27=makeQuery(id+"F2.imprint","IMPRINT",FACE,{"disambiguationData":[TD([[makeQuery(id+"F2.imprint","IMPRINT",EDGE,{"disambiguationData":[TD([[subQ2,-1.0]])],"derivedFrom":subQ1}),-1.0]])]});}
            var Q28;
            {var subQ0=sQuery(id+"F2.wireOp",EDGE,"E96");var subQ1=sQuery(id+"F2.wireOp",EDGE,"E78");var subQ2=makeQuery(id+"F2.imprint","INTERSECT",VERTEX,{"derivedFrom":[subQ1,subQ0]});Q28=makeQuery(id+"F2.imprint","IMPRINT",FACE,{"disambiguationData":[TD([[makeQuery(id+"F2.imprint","IMPRINT",EDGE,{"disambiguationData":[TD([[subQ2,-1.0]])],"derivedFrom":subQ1}),-1.0]])]});}
            var Q29;
            {var subQ0=sQuery(id+"F2.wireOp",EDGE,"E95");var subQ1=sQuery(id+"F2.wireOp",EDGE,"E77");var subQ2=makeQuery(id+"F2.imprint","INTERSECT",VERTEX,{"derivedFrom":[subQ1,subQ0]});Q29=makeQuery(id+"F2.imprint","IMPRINT",FACE,{"disambiguationData":[TD([[makeQuery(id+"F2.imprint","IMPRINT",EDGE,{"disambiguationData":[TD([[subQ2,-1.0]])],"derivedFrom":subQ1}),1.0]])]});}
            var Q30;
            {var subQ0=sQuery(id+"F2.wireOp",EDGE,"E95");var subQ1=sQuery(id+"F2.wireOp",EDGE,"E79");var subQ2=makeQuery(id+"F2.imprint","INTERSECT",VERTEX,{"derivedFrom":[subQ1,subQ0]});Q30=makeQuery(id+"F2.imprint","IMPRINT",FACE,{"disambiguationData":[TD([[makeQuery(id+"F2.imprint","IMPRINT",EDGE,{"disambiguationData":[TD([[subQ2,-1.0]])],"derivedFrom":subQ1}),1.0]])]});}
            var Q31;
            {var subQ0=sQuery(id+"F2.wireOp",EDGE,"E97");var subQ1=sQuery(id+"F2.wireOp",EDGE,"E77");var subQ2=makeQuery(id+"F2.imprint","INTERSECT",VERTEX,{"derivedFrom":[subQ1,subQ0]});Q31=makeQuery(id+"F2.imprint","IMPRINT",FACE,{"disambiguationData":[TD([[makeQuery(id+"F2.imprint","IMPRINT",EDGE,{"disambiguationData":[TD([[subQ2,-1.0]])],"derivedFrom":subQ1}),1.0]])]});}
            var Q32;
            {var subQ0=sQuery(id+"F2.wireOp",EDGE,"E97");var subQ1=sQuery(id+"F2.wireOp",EDGE,"E79");var subQ2=makeQuery(id+"F2.imprint","INTERSECT",VERTEX,{"derivedFrom":[subQ1,subQ0]});Q32=makeQuery(id+"F2.imprint","IMPRINT",FACE,{"disambiguationData":[TD([[makeQuery(id+"F2.imprint","IMPRINT",EDGE,{"disambiguationData":[TD([[subQ2,-1.0]])],"derivedFrom":subQ1}),1.0]])]});}
            var Q33;
            {var subQ0=sQuery(id+"F2.wireOp",EDGE,"E80");var subQ1=sQuery(id+"F2.wireOp",EDGE,"E54");var subQ2=makeQuery(id+"F2.imprint","INTERSECT",VERTEX,{"derivedFrom":[subQ1,subQ0]});Q33=makeQuery(id+"F2.imprint","IMPRINT",FACE,{"disambiguationData":[TD([[makeQuery(id+"F2.imprint","IMPRINT",EDGE,{"disambiguationData":[TD([[subQ2,-1.0]])],"derivedFrom":subQ1}),-1.0]])]});}
            var Q34;
            {var subQ0=sQuery(id+"F2.wireOp",EDGE,"E99");var subQ1=sQuery(id+"F2.wireOp",EDGE,"E80");var subQ2=makeQuery(id+"F2.imprint","INTERSECT",VERTEX,{"derivedFrom":[subQ1,subQ0]});Q34=makeQuery(id+"F2.imprint","IMPRINT",FACE,{"disambiguationData":[TD([[makeQuery(id+"F2.imprint","IMPRINT",EDGE,{"disambiguationData":[TD([[subQ2,-1.0]])],"derivedFrom":subQ1}),-1.0]])]});}
            var Q35;
            {var subQ0=sQuery(id+"F2.wireOp",EDGE,"E96");var subQ1=sQuery(id+"F2.wireOp",EDGE,"E80");var subQ2=makeQuery(id+"F2.imprint","INTERSECT",VERTEX,{"derivedFrom":[subQ1,subQ0]});Q35=makeQuery(id+"F2.imprint","IMPRINT",FACE,{"disambiguationData":[TD([[makeQuery(id+"F2.imprint","IMPRINT",EDGE,{"disambiguationData":[TD([[subQ2,-1.0]])],"derivedFrom":subQ1}),-1.0]])]});}
            var Q36;
            {var subQ0=sQuery(id+"F2.wireOp",EDGE,"E103");var subQ1=sQuery(id+"F2.wireOp",EDGE,"E72");var subQ2=makeQuery(id+"F2.imprint","INTERSECT",VERTEX,{"derivedFrom":[subQ1,subQ0]});Q36=makeQuery(id+"F2.imprint","IMPRINT",FACE,{"disambiguationData":[TD([[makeQuery(id+"F2.imprint","IMPRINT",EDGE,{"disambiguationData":[TD([[subQ2,-1.0]])],"derivedFrom":subQ1}),1.0]])]});}
            var Q37;
            {var subQ0=sQuery(id+"F2.wireOp",EDGE,"E103");var subQ1=sQuery(id+"F2.wireOp",EDGE,"E72");var subQ2=makeQuery(id+"F2.imprint","INTERSECT",VERTEX,{"derivedFrom":[subQ1,subQ0]});Q37=makeQuery(id+"F2.imprint","IMPRINT",FACE,{"disambiguationData":[TD([[makeQuery(id+"F2.imprint","IMPRINT",EDGE,{"disambiguationData":[TD([[subQ2,-1.0]])],"derivedFrom":subQ1}),-1.0]])]});}
            var Q38;
            {var subQ0=sQuery(id+"F2.wireOp",EDGE,"E102");var subQ1=sQuery(id+"F2.wireOp",EDGE,"E73");var subQ2=makeQuery(id+"F2.imprint","INTERSECT",VERTEX,{"derivedFrom":[subQ1,subQ0]});Q38=makeQuery(id+"F2.imprint","IMPRINT",FACE,{"disambiguationData":[TD([[makeQuery(id+"F2.imprint","IMPRINT",EDGE,{"disambiguationData":[TD([[subQ2,-1.0]])],"derivedFrom":subQ1}),1.0]])]});}
            var Q39;
            {var subQ0=sQuery(id+"F2.wireOp",EDGE,"E97");var subQ1=sQuery(id+"F2.wireOp",EDGE,"E74");var subQ2=makeQuery(id+"F2.imprint","INTERSECT",VERTEX,{"derivedFrom":[subQ1,subQ0]});Q39=makeQuery(id+"F2.imprint","IMPRINT",FACE,{"disambiguationData":[TD([[makeQuery(id+"F2.imprint","IMPRINT",EDGE,{"disambiguationData":[TD([[subQ2,-1.0]])],"derivedFrom":subQ1}),1.0]])]});}
            var Q40;
            {var subQ4=sQuery(id+"F2.wireOp",EDGE,"E75");var subQ6=sQuery(id+"F2.wireOp",EDGE,"E51");var subQ9=makeQuery(id+"F2.imprint","INTERSECT",VERTEX,{"derivedFrom":[subQ6,subQ4]});Q40=makeQuery(id+"F2.imprint","IMPRINT",FACE,{"disambiguationData":[TD([[makeQuery(id+"F2.imprint","IMPRINT",EDGE,{"disambiguationData":[TD([[subQ9,1.0]])],"derivedFrom":subQ6}),-1.0]])]});}
            var Q41;
            {var subQ0=sQuery(id+"F2.wireOp",EDGE,"E72");var subQ1=sQuery(id+"F2.wireOp",EDGE,"E51");var subQ2=makeQuery(id+"F2.imprint","INTERSECT",VERTEX,{"derivedFrom":[subQ1,subQ0]});Q41=makeQuery(id+"F2.imprint","IMPRINT",FACE,{"disambiguationData":[TD([[makeQuery(id+"F2.imprint","IMPRINT",EDGE,{"disambiguationData":[TD([[subQ2,1.0]])],"derivedFrom":subQ1}),-1.0]])]});}
            var Q42;
            {var subQ0=sQuery(id+"F2.wireOp",EDGE,"E80");var subQ1=sQuery(id+"F2.wireOp",EDGE,"E51");var subQ2=makeQuery(id+"F2.imprint","INTERSECT",VERTEX,{"derivedFrom":[subQ1,subQ0]});Q42=makeQuery(id+"F2.imprint","IMPRINT",FACE,{"disambiguationData":[TD([[makeQuery(id+"F2.imprint","IMPRINT",EDGE,{"disambiguationData":[TD([[subQ2,1.0]])],"derivedFrom":subQ1}),-1.0]])]});}
            var Q43;
            {var subQ0=sQuery(id+"F2.wireOp",EDGE,"E80");var subQ1=sQuery(id+"F2.wireOp",EDGE,"E54");var subQ2=makeQuery(id+"F2.imprint","INTERSECT",VERTEX,{"derivedFrom":[subQ1,subQ0]});Q43=makeQuery(id+"F2.imprint","IMPRINT",FACE,{"disambiguationData":[TD([[makeQuery(id+"F2.imprint","IMPRINT",EDGE,{"disambiguationData":[TD([[subQ2,-1.0]])],"derivedFrom":subQ1}),-1.0]])]});}
            var Q44;
            {var subQ0=sQuery(id+"F2.wireOp",EDGE,"E99");var subQ1=sQuery(id+"F2.wireOp",EDGE,"E80");var subQ2=makeQuery(id+"F2.imprint","INTERSECT",VERTEX,{"derivedFrom":[subQ1,subQ0]});Q44=makeQuery(id+"F2.imprint","IMPRINT",FACE,{"disambiguationData":[TD([[makeQuery(id+"F2.imprint","IMPRINT",EDGE,{"disambiguationData":[TD([[subQ2,-1.0]])],"derivedFrom":subQ1}),-1.0]])]});}
            var Q45;
            {var subQ0=sQuery(id+"F2.wireOp",EDGE,"E96");var subQ1=sQuery(id+"F2.wireOp",EDGE,"E80");var subQ2=makeQuery(id+"F2.imprint","INTERSECT",VERTEX,{"derivedFrom":[subQ1,subQ0]});Q45=makeQuery(id+"F2.imprint","IMPRINT",FACE,{"disambiguationData":[TD([[makeQuery(id+"F2.imprint","IMPRINT",EDGE,{"disambiguationData":[TD([[subQ2,-1.0]])],"derivedFrom":subQ1}),-1.0]])]});}
            var Q46;
            {var subQ0=sQuery(id+"F2.wireOp",EDGE,"E78");var subQ1=sQuery(id+"F2.wireOp",EDGE,"E51");var subQ2=makeQuery(id+"F2.imprint","INTERSECT",VERTEX,{"derivedFrom":[subQ1,subQ0]});Q46=makeQuery(id+"F2.imprint","IMPRINT",FACE,{"disambiguationData":[TD([[makeQuery(id+"F2.imprint","IMPRINT",EDGE,{"disambiguationData":[TD([[subQ2,1.0]])],"derivedFrom":subQ1}),-1.0]])]});}
            var Q47;
            {var subQ0=sQuery(id+"F2.wireOp",EDGE,"E78");var subQ1=sQuery(id+"F2.wireOp",EDGE,"E54");var subQ2=makeQuery(id+"F2.imprint","INTERSECT",VERTEX,{"derivedFrom":[subQ1,subQ0]});Q47=makeQuery(id+"F2.imprint","IMPRINT",FACE,{"disambiguationData":[TD([[makeQuery(id+"F2.imprint","IMPRINT",EDGE,{"disambiguationData":[TD([[subQ2,-1.0]])],"derivedFrom":subQ1}),-1.0]])]});}
            var Q48;
            {var subQ0=sQuery(id+"F2.wireOp",EDGE,"E99");var subQ1=sQuery(id+"F2.wireOp",EDGE,"E78");var subQ2=makeQuery(id+"F2.imprint","INTERSECT",VERTEX,{"derivedFrom":[subQ1,subQ0]});Q48=makeQuery(id+"F2.imprint","IMPRINT",FACE,{"disambiguationData":[TD([[makeQuery(id+"F2.imprint","IMPRINT",EDGE,{"disambiguationData":[TD([[subQ2,-1.0]])],"derivedFrom":subQ1}),-1.0]])]});}
            var Q49;
            {var subQ0=sQuery(id+"F2.wireOp",EDGE,"E96");var subQ1=sQuery(id+"F2.wireOp",EDGE,"E78");var subQ2=makeQuery(id+"F2.imprint","INTERSECT",VERTEX,{"derivedFrom":[subQ1,subQ0]});Q49=makeQuery(id+"F2.imprint","IMPRINT",FACE,{"disambiguationData":[TD([[makeQuery(id+"F2.imprint","IMPRINT",EDGE,{"disambiguationData":[TD([[subQ2,-1.0]])],"derivedFrom":subQ1}),-1.0]])]});}
            var Q50;
            {var subQ0=sQuery(id+"F2.wireOp",EDGE,"E76");var subQ1=sQuery(id+"F2.wireOp",EDGE,"E51");var subQ2=makeQuery(id+"F2.imprint","INTERSECT",VERTEX,{"derivedFrom":[subQ1,subQ0]});Q50=makeQuery(id+"F2.imprint","IMPRINT",FACE,{"disambiguationData":[TD([[makeQuery(id+"F2.imprint","IMPRINT",EDGE,{"disambiguationData":[TD([[subQ2,1.0]])],"derivedFrom":subQ1}),-1.0]])]});}
            var Q51;
            {var subQ0=sQuery(id+"F2.wireOp",EDGE,"E76");var subQ1=sQuery(id+"F2.wireOp",EDGE,"E54");var subQ2=makeQuery(id+"F2.imprint","INTERSECT",VERTEX,{"derivedFrom":[subQ1,subQ0]});Q51=makeQuery(id+"F2.imprint","IMPRINT",FACE,{"disambiguationData":[TD([[makeQuery(id+"F2.imprint","IMPRINT",EDGE,{"disambiguationData":[TD([[subQ2,-1.0]])],"derivedFrom":subQ1}),-1.0]])]});}
            var Q52;
            {var subQ0=sQuery(id+"F2.wireOp",EDGE,"E97");var subQ1=sQuery(id+"F2.wireOp",EDGE,"E76");var subQ2=makeQuery(id+"F2.imprint","INTERSECT",VERTEX,{"derivedFrom":[subQ1,subQ0]});Q52=makeQuery(id+"F2.imprint","IMPRINT",FACE,{"disambiguationData":[TD([[makeQuery(id+"F2.imprint","IMPRINT",EDGE,{"disambiguationData":[TD([[subQ2,-1.0]])],"derivedFrom":subQ1}),1.0]])]});}
            var Q53;
            {var subQ0=sQuery(id+"F2.wireOp",EDGE,"E95");var subQ1=sQuery(id+"F2.wireOp",EDGE,"E76");var subQ2=makeQuery(id+"F2.imprint","INTERSECT",VERTEX,{"derivedFrom":[subQ1,subQ0]});Q53=makeQuery(id+"F2.imprint","IMPRINT",FACE,{"disambiguationData":[TD([[makeQuery(id+"F2.imprint","IMPRINT",EDGE,{"disambiguationData":[TD([[subQ2,-1.0]])],"derivedFrom":subQ1}),1.0]])]});}
            var Q54;
            {var subQ22=sQuery(id+"F2.wireOp",EDGE,"E58");Q54=makeQuery(id+"F2.imprint","IMPRINT",FACE,{"disambiguationData":[TD([[makeQuery(id+"F2.imprint","IMPRINT",EDGE,{"derivedFrom":subQ22}),1.0]])]});}
            var Q55;
            {var subQ0=sQuery(id+"F2.wireOp",EDGE,"E87");Q55=makeQuery(id+"F2.imprint","IMPRINT",FACE,{"disambiguationData":[TD([[makeQuery(id+"F2.imprint","IMPRINT",EDGE,{"derivedFrom":subQ0}),-1.0]])]});}
            var Q56;
            {var subQ0=sQuery(id+"F2.wireOp",EDGE,"E86");Q56=makeQuery(id+"F2.imprint","IMPRINT",FACE,{"disambiguationData":[TD([[makeQuery(id+"F2.imprint","IMPRINT",EDGE,{"derivedFrom":subQ0}),1.0]])]});}
            var Q57;
            {var subQ0=sQuery(id+"F2.wireOp",EDGE,"E153");Q57=makeQuery(id+"F2.imprint","IMPRINT",FACE,{"disambiguationData":[TD([[makeQuery(id+"F2.imprint","IMPRINT",EDGE,{"derivedFrom":subQ0}),1.0]])]});}
            var Q58;
            {var subQ0=sQuery(id+"F2.wireOp",EDGE,"E89");Q58=makeQuery(id+"F2.imprint","IMPRINT",FACE,{"disambiguationData":[TD([[makeQuery(id+"F2.imprint","IMPRINT",EDGE,{"derivedFrom":subQ0}),1.0]])]});}
            var Q59;
            {var subQ0=sQuery(id+"F2.wireOp",EDGE,"E97");var subQ1=sQuery(id+"F2.wireOp",EDGE,"E81");var subQ2=makeQuery(id+"F2.imprint","INTERSECT",VERTEX,{"derivedFrom":[subQ1,subQ0]});Q59=makeQuery(id+"F2.imprint","IMPRINT",FACE,{"disambiguationData":[TD([[makeQuery(id+"F2.imprint","IMPRINT",EDGE,{"disambiguationData":[TD([[subQ2,-1.0]])],"derivedFrom":subQ1}),1.0]])]});}
            extrude(context, id + "F3", {"entities" : qUnion([Q0, Q1, Q2, Q3, Q4, Q5, Q6, Q7, Q8, Q9, Q10, Q11, Q12, Q13, Q14, Q15, Q16, Q17, Q18, Q19, Q20, Q21, Q22, Q23, Q24, Q25, Q26, Q27, Q28, Q29, Q30, Q31, Q32, Q33, Q34, Q35, Q36, Q37, Q38, Q39, Q40, Q41, Q42, Q43, Q44, Q45, Q46, Q47, Q48, Q49, Q50, Q51, Q52, Q53, Q54, Q55, Q56, Q57, Q58, Q59]), "depth" : 45 * mm, "offsetDistance" : 25 * mm});
        }
        {
            var Q0;
            Q0=makeQuery(id+"F3.opExtrude","CAP_FACE",FACE,{"disambiguationData":[OSD([sQuery(id+"F2.wireOp",EDGE,"E50"),sQuery(id+"F2.wireOp",EDGE,"E51"),sQuery(id+"F2.wireOp",EDGE,"E52"),sQuery(id+"F2.wireOp",EDGE,"E53"),sQuery(id+"F2.wireOp",EDGE,"E54"),sQuery(id+"F2.wireOp",EDGE,"E55"),sQuery(id+"F2.wireOp",EDGE,"E56"),sQuery(id+"F2.wireOp",EDGE,"E57"),sQuery(id+"F2.wireOp",EDGE,"E59"),sQuery(id+"F2.wireOp",EDGE,"E60"),sQuery(id+"F2.wireOp",EDGE,"E61"),sQuery(id+"F2.wireOp",EDGE,"E62"),sQuery(id+"F2.wireOp",EDGE,"E63"),sQuery(id+"F2.wireOp",EDGE,"E64"),sQuery(id+"F2.wireOp",EDGE,"E65"),sQuery(id+"F2.wireOp",EDGE,"E66"),sQuery(id+"F2.wireOp",EDGE,"E67"),sQuery(id+"F2.wireOp",EDGE,"E68"),sQuery(id+"F2.wireOp",EDGE,"E69"),sQuery(id+"F2.wireOp",EDGE,"E70"),sQuery(id+"F2.wireOp",EDGE,"E71"),sQuery(id+"F2.wireOp",EDGE,"E72"),sQuery(id+"F2.wireOp",EDGE,"E73"),sQuery(id+"F2.wireOp",EDGE,"E74"),sQuery(id+"F2.wireOp",EDGE,"E75"),sQuery(id+"F2.wireOp",EDGE,"E76"),sQuery(id+"F2.wireOp",EDGE,"E77"),sQuery(id+"F2.wireOp",EDGE,"E78"),sQuery(id+"F2.wireOp",EDGE,"E79"),sQuery(id+"F2.wireOp",EDGE,"E80"),sQuery(id+"F2.wireOp",EDGE,"E81"),sQuery(id+"F2.wireOp",EDGE,"E82"),sQuery(id+"F2.wireOp",EDGE,"E83"),sQuery(id+"F2.wireOp",EDGE,"E84"),sQuery(id+"F2.wireOp",EDGE,"E85"),sQuery(id+"F2.wireOp",EDGE,"E86"),sQuery(id+"F2.wireOp",EDGE,"E87"),sQuery(id+"F2.wireOp",EDGE,"E88.trimOffspring"),sQuery(id+"F2.wireOp",EDGE,"E89"),sQuery(id+"F2.wireOp",EDGE,"3ceda469-106e-433b-afd7-72ab2decd5a5"),sQuery(id+"F2.wireOp",EDGE,"E90"),sQuery(id+"F2.wireOp",EDGE,"E91"),sQuery(id+"F2.wireOp",EDGE,"E92"),sQuery(id+"F2.wireOp",EDGE,"E93"),sQuery(id+"F2.wireOp",EDGE,"E94"),sQuery(id+"F2.wireOp",EDGE,"E95"),sQuery(id+"F2.wireOp",EDGE,"E96"),sQuery(id+"F2.wireOp",EDGE,"E97"),sQuery(id+"F2.wireOp",EDGE,"E98"),sQuery(id+"F2.wireOp",EDGE,"E99"),sQuery(id+"F2.wireOp",EDGE,"E100"),sQuery(id+"F2.wireOp",EDGE,"E101"),sQuery(id+"F2.wireOp",EDGE,"E102"),sQuery(id+"F2.wireOp",EDGE,"E103")])],"isStart":false});
            var sketch = newSketch(context, id + "F4", { "sketchPlane" : qUnion([Q0])});
            skLineSegment(sketch, "E156.bottom", {"start": v(5555, 2165) * mm, "end": v(7410, 2165) * mm});
            skLineSegment(sketch, "E156.top", {"start": v(5555, 200) * mm, "end": v(7410, 200) * mm});
            skLineSegment(sketch, "E156.left", {"start": v(7410, 2165) * mm, "end": v(7410, 200) * mm});
            skLineSegment(sketch, "E156.right", {"start": v(5555, 2165) * mm, "end": v(5555, 200) * mm});
            skLineSegment(sketch, "E157.bottom", {"start": v(5645, 2165) * mm, "end": v(7400, 2165) * mm});
            skLineSegment(sketch, "E157.top", {"start": v(5645, 1090) * mm, "end": v(7400, 1090) * mm});
            skLineSegment(sketch, "E157.left", {"start": v(5645, 2165) * mm, "end": v(5645, 1090) * mm});
            skLineSegment(sketch, "E157.right", {"start": v(7400, 2165) * mm, "end": v(7400, 1090) * mm});
            skSolve(sketch);
        }
        {
            var Q0;
            Q0 = qSketchRegion(id + "F4", true);
            extrude(context, id + "F5", {"entities" : qUnion([Q0]), "operationType" : NewBodyOperationType.REMOVE, "oppositeDirection" : true, "depth" : 60 * mm, "offsetDistance" : 25 * mm});
        }
    });
